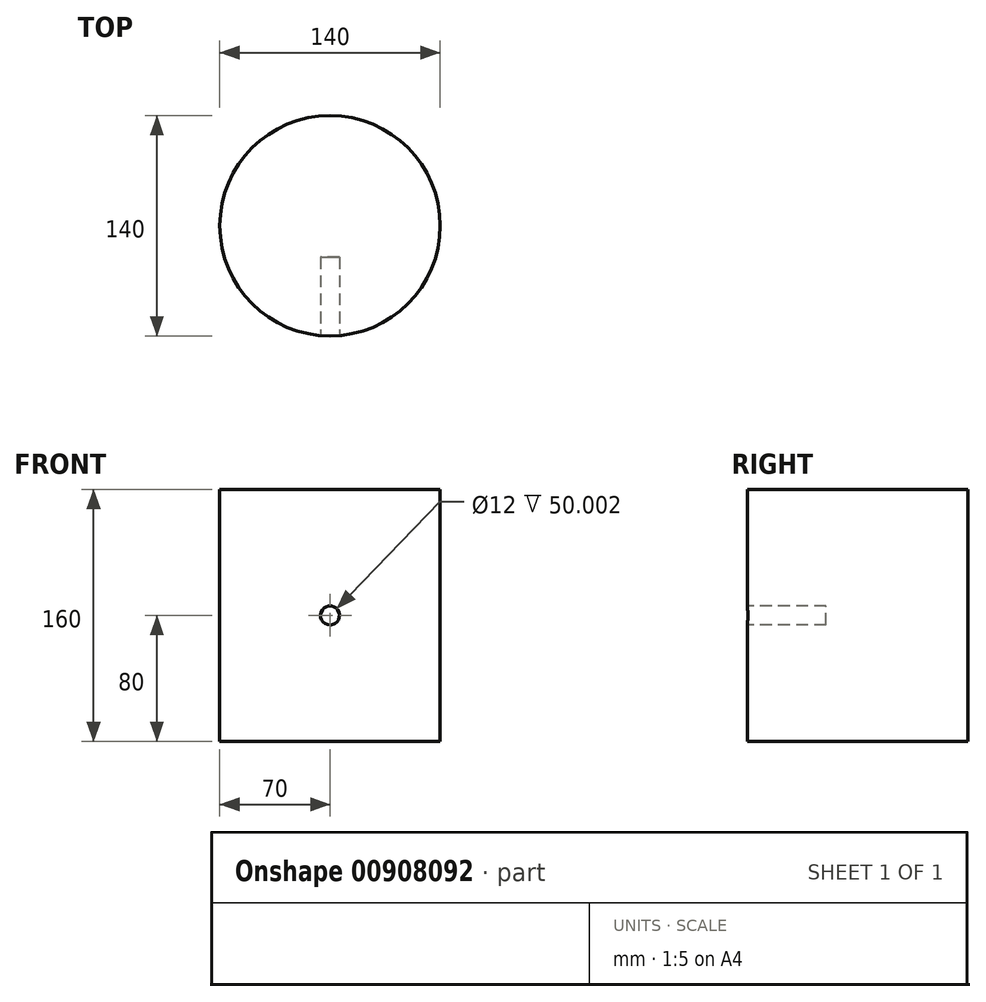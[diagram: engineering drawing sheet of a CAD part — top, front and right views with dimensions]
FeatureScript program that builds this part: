
annotation { "Feature Type Name" : "Feature", "Feature Type Description" : "" }
export const myFeature = defineFeature(function(context is Context, id is Id, definition is map)
    precondition{}
    {
        {
            var Q0;
            Q0=qCreatedBy(makeId("Top.planeOp"),FACE);
            var sketch = newSketch(context, id + "F0", { "sketchPlane" : qUnion([Q0])});
            skCircle(sketch, "E0", {"center": v(0, 0) * mm, "radius": 70 * mm});
            skSolve(sketch);
        }
        {
            var Q0;
            Q0 = qSketchRegion(id + "F0", true);
            extrude(context, id + "F1", {"entities" : qUnion([Q0]), "depth" : 160 * mm, "offsetDistance" : 25 * mm});
        }
        {
            var Q0;
            Q0=qCreatedBy(makeId("Front.planeOp"),FACE);
            cPlane(context, id + "F2", {"entities" : qUnion([Q0]), "cplaneType" : CPlaneType.OFFSET, "offset" : 70 * mm, "width" : 150 * mm, "height" : 150 * mm});
        }
        {
            var Q0;
            Q0=qCreatedBy(id+"F2.planeOp",FACE);
            var sketch = newSketch(context, id + "F3", { "sketchPlane" : qUnion([Q0])});
            skCircle(sketch, "E1", {"center": v(0, 80) * mm, "radius": 6 * mm});
            skLineSegment(sketch, "E2", {"start": v(0, 160) * mm, "end": v(0, 0) * mm, "construction": true});
            skSolve(sketch);
        }
        {
            var Q0;
            Q0=makeQuery(id+"F3.imprint","IMPRINT",FACE,{"disambiguationData":[TD([[makeQuery(id+"F3.imprint","IMPRINT",EDGE,{"derivedFrom":sQuery(id+"F3.wireOp",EDGE,"E1")}),1.0]])]});
            var Q1;
            Q1=sQuery(id+"F3.wireOp",EDGE,"E1");
            extrude(context, id + "F4", {"entities" : qUnion([Q0]), "operationType" : NewBodyOperationType.REMOVE, "surfaceEntities" : qUnion([Q1]), "oppositeDirection" : true, "depth" : 50 * mm, "offsetDistance" : 25 * mm});
        }
    });
